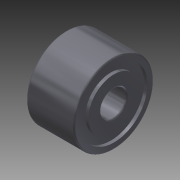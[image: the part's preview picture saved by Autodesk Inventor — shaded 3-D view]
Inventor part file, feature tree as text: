
AUTODESK INVENTOR PART (.ipt)
format: ipt  version: 2012 (Build 160160000, 160)  size: 142,336 bytes
history: native  units: in
note: dims shown in document units (in); Inventor stores cm internally (conversion verified against a paired STEP export)
features: revolve x1, fillet x1, sketch x1
ambient origin geometry x8: Origin, YZ Plane, XZ Plane, XY Plane, X Axis, Y Axis, Z Axis, Center Point
bodies: Solid1 (feature_tree)
feature tree (3):
  revolve  "Revolution1"  [1 undecoded]
  fillet  "Fillet1"  Radius=0.0625in
  sketch  "Sketch1"  dims[d0=0.25in d1=0.1875in d2=0.0625in d3=0.3125in d5=0.4375in d6=0.375in d7=0.05in d8=0.0625in d9=0.1in d10=0.025in d11=90.0deg d12=0.0125in]
note: 1 required parameter value undecoded (feature->parameter linkage not recoverable at this tier; creation-order binding heuristic only, values carry confidence <= 0.55)
